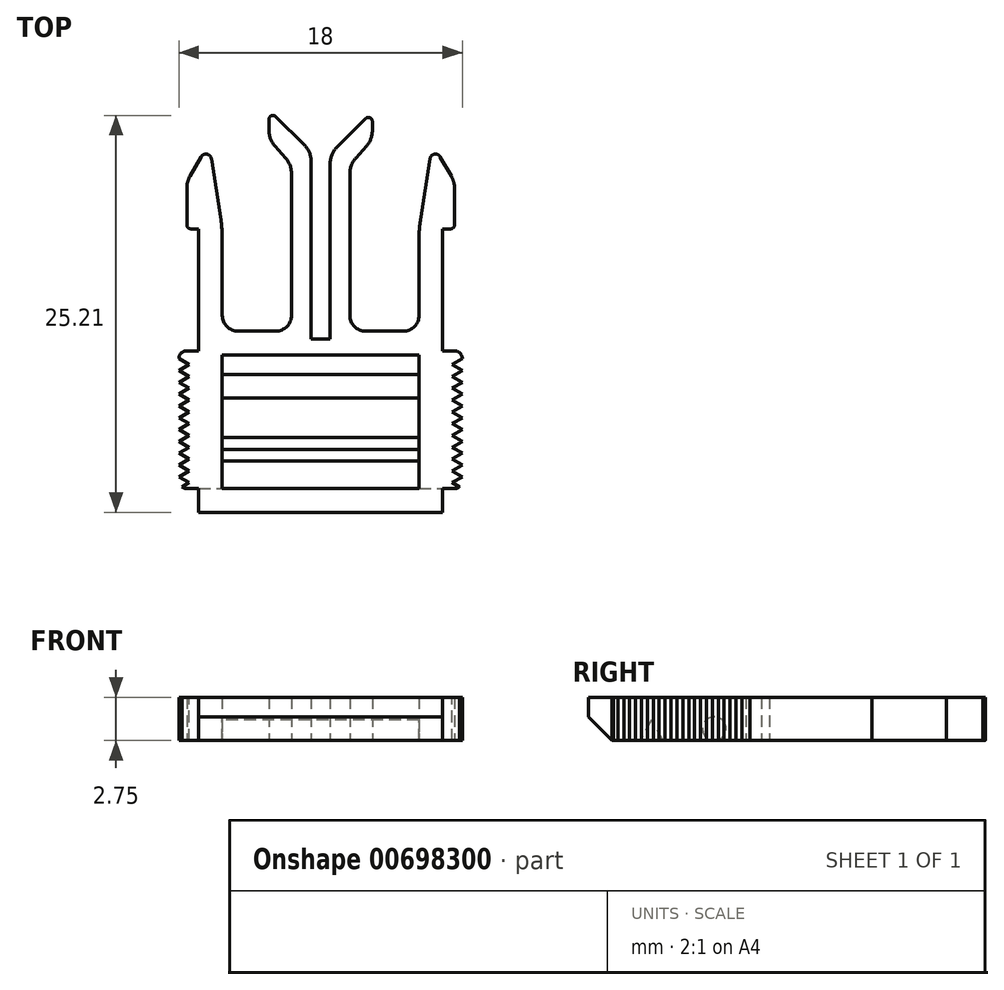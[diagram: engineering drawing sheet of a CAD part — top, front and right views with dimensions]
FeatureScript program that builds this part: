
annotation { "Feature Type Name" : "Feature", "Feature Type Description" : "" }
export const myFeature = defineFeature(function(context is Context, id is Id, definition is map)
    precondition{}
    {
        {
            var Q0;
            Q0=qCreatedBy(makeId("Top.planeOp"),FACE);
            var sketch = newSketch(context, id + "F0", { "sketchPlane" : qUnion([Q0])});
            skLineSegment(sketch, "E0.top", {"start": v(15.5, -24.35) * mm, "end": v(-15.5, -24.35) * mm});
            skPoint(sketch, "E0.middle", {"position": v(0, 0) * mm});
            skLineSegment(sketch, "E1.bottom", {"start": v(12.5, -4.35) * mm, "end": v(-12.5, -4.35) * mm});
            skLineSegment(sketch, "E1.top", {"start": v(12.5, -21.35) * mm, "end": v(-12.5, -21.35) * mm});
            skLineSegment(sketch, "E1.left", {"start": v(12.5, -4.35) * mm, "end": v(12.5, -21.35) * mm});
            skLineSegment(sketch, "E1.right", {"start": v(-12.5, -4.35) * mm, "end": v(-12.5, -21.35) * mm});
            skPoint(sketch, "E1.middle", {"position": v(0, -12.85) * mm});
            skLineSegment(sketch, "E2", {"start": v(15.18, 20.8) * mm, "end": v(16.6, 18.34) * mm});
            skLineSegment(sketch, "E3", {"start": v(17, 16.84) * mm, "end": v(17, 12.15) * mm});
            skLineSegment(sketch, "E4", {"start": v(16.5, 11.65) * mm, "end": v(15.5, 11.65) * mm});
            skLineSegment(sketch, "E5", {"start": v(0, -4.35) * mm, "end": v(0, 27.9) * mm, "construction": true});
            skLineSegment(sketch, "E6", {"start": v(-10.5, -1.35) * mm, "end": v(-5.7, -1.35) * mm});
            skLineSegment(sketch, "E7.trimOffspring", {"start": v(15.5, 11.65) * mm, "end": v(15.5, -24.35) * mm});
            skLineSegment(sketch, "E8", {"start": v(12.5, 10.49) * mm, "end": v(12.5, 0.65) * mm});
            skLineSegment(sketch, "E9.0", {"start": v(-3.7, 0.65) * mm, "end": v(-3.7, 18.65) * mm});
            skLineSegment(sketch, "E10.0", {"start": v(3.7, 0.65) * mm, "end": v(3.7, 18.65) * mm});
            skLineSegment(sketch, "E11", {"start": v(13.89, 20.55) * mm, "end": v(12.68, 12.8) * mm});
            skPoint(sketch, "E12.visualSharp", {"position": v(12.5, 11.65) * mm});
            skArc(sketch, "E12.filletArc", {"start": v(12.68, 12.8) * mm, "mid": v(12.54, 11.64) * mm, "end": v(12.5, 10.49) * mm});
            skLineSegment(sketch, "E13.trimOffspring", {"start": v(5.7, -1.35) * mm, "end": v(10.5, -1.35) * mm});
            skPoint(sketch, "E14.orphan", {"position": v(13.51, 18.14) * mm});
            skPoint(sketch, "E15.orphan", {"position": v(16.29, 18.88) * mm});
            skPoint(sketch, "E16.orphan", {"position": v(15.5, -1.35) * mm});
            skPoint(sketch, "E17.visualSharp", {"position": v(14.2, 22.51) * mm});
            skArc(sketch, "E17.filletArc", {"start": v(15.18, 20.8) * mm, "mid": v(14.45, 21.13) * mm, "end": v(13.89, 20.55) * mm});
            skArc(sketch, "E18.MirrorCS", {"start": v(-15.18, 20.8) * mm, "mid": v(-14.45, 21.13) * mm, "end": v(-13.89, 20.55) * mm});
            skLineSegment(sketch, "E19.MirrorCS", {"start": v(-15.18, 20.8) * mm, "end": v(-16.6, 18.34) * mm});
            skLineSegment(sketch, "E20.MirrorCS", {"start": v(-16.5, 11.65) * mm, "end": v(-15.5, 11.65) * mm});
            skPoint(sketch, "E21.MirrorP", {"position": v(-13.51, 18.14) * mm});
            skPoint(sketch, "E22.MirrorP", {"position": v(-12.5, 11.65) * mm});
            skArc(sketch, "E23.MirrorCS", {"start": v(-12.68, 12.8) * mm, "mid": v(-12.54, 11.64) * mm, "end": v(-12.5, 10.49) * mm});
            skPoint(sketch, "E24.MirrorP", {"position": v(-14.2, 22.51) * mm});
            skPoint(sketch, "E25.MirrorP", {"position": v(-16.29, 18.88) * mm});
            skLineSegment(sketch, "E26.MirrorCS", {"start": v(-17, 16.84) * mm, "end": v(-17, 12.15) * mm});
            skLineSegment(sketch, "E27.MirrorCS", {"start": v(-13.89, 20.55) * mm, "end": v(-12.68, 12.8) * mm});
            skLineSegment(sketch, "E28.MirrorCS", {"start": v(-15.5, 11.65) * mm, "end": v(-15.5, -24.35) * mm});
            skLineSegment(sketch, "E29.MirrorCS", {"start": v(-12.5, 10.49) * mm, "end": v(-12.5, 0.65) * mm});
            skLineSegment(sketch, "E30.0", {"start": v(1.2, -2.35) * mm, "end": v(1.2, 19.9) * mm});
            skLineSegment(sketch, "E31.0", {"start": v(-1.2, -2.35) * mm, "end": v(-1.2, 20.17) * mm});
            skLineSegment(sketch, "E32", {"start": v(5.7, 25.65) * mm, "end": v(2.08, 22.03) * mm});
            skLineSegment(sketch, "E33", {"start": v(-5.7, 25.92) * mm, "end": v(-2.08, 22.29) * mm});
            skPoint(sketch, "E34.visualSharp", {"position": v(17, 17.65) * mm});
            skArc(sketch, "E34.filletArc", {"start": v(17, 16.84) * mm, "mid": v(16.9, 17.62) * mm, "end": v(16.6, 18.34) * mm});
            skPoint(sketch, "E35.visualSharp", {"position": v(-17, 17.65) * mm});
            skArc(sketch, "E35.filletArc", {"start": v(-16.6, 18.34) * mm, "mid": v(-16.9, 17.62) * mm, "end": v(-17, 16.84) * mm});
            skLineSegment(sketch, "E36", {"start": v(-1.2, -2.35) * mm, "end": v(1.2, -2.35) * mm});
            skPoint(sketch, "E37.orphan", {"position": v(1.2, 0.65) * mm});
            skPoint(sketch, "E38.orphan", {"position": v(-1.2, 0.65) * mm});
            skLineSegment(sketch, "E39", {"start": v(4.46, 20.65) * mm, "end": v(5.8, 22.14) * mm});
            skLineSegment(sketch, "E40", {"start": v(6.56, 24.14) * mm, "end": v(6.56, 25.3) * mm});
            skLineSegment(sketch, "E41.MirrorCS", {"start": v(-4.46, 20.65) * mm, "end": v(-5.8, 22.14) * mm});
            skLineSegment(sketch, "E42.MirrorCS", {"start": v(-6.56, 24.14) * mm, "end": v(-6.56, 25.56) * mm});
            skPoint(sketch, "E43.newPointB", {"position": v(6.56, 27.77) * mm});
            skArc(sketch, "E43.filletArc", {"start": v(6.56, 25.3) * mm, "mid": v(6.25, 25.76) * mm, "end": v(5.7, 25.65) * mm});
            skPoint(sketch, "E44.newPointB", {"position": v(-6.56, 27.77) * mm});
            skArc(sketch, "E44.filletArc", {"start": v(-5.7, 25.92) * mm, "mid": v(-6.25, 26.03) * mm, "end": v(-6.56, 25.56) * mm});
            skPoint(sketch, "E45.orphan", {"position": v(3.7, 23.65) * mm});
            skPoint(sketch, "E46.orphan", {"position": v(-3.7, 23.91) * mm});
            skPoint(sketch, "E47.visualSharp", {"position": v(3.7, 19.8) * mm});
            skArc(sketch, "E47.filletArc", {"start": v(4.46, 20.65) * mm, "mid": v(3.9, 19.72) * mm, "end": v(3.7, 18.65) * mm});
            skPoint(sketch, "E48.visualSharp", {"position": v(1.2, 21.15) * mm});
            skArc(sketch, "E48.filletArc", {"start": v(2.08, 22.03) * mm, "mid": v(1.43, 21.05) * mm, "end": v(1.2, 19.9) * mm});
            skPoint(sketch, "E49.visualSharp", {"position": v(-1.2, 21.41) * mm});
            skArc(sketch, "E49.filletArc", {"start": v(-1.2, 20.17) * mm, "mid": v(-1.43, 21.32) * mm, "end": v(-2.08, 22.29) * mm});
            skPoint(sketch, "E50.visualSharp", {"position": v(-3.7, 19.8) * mm});
            skArc(sketch, "E50.filletArc", {"start": v(-3.7, 18.65) * mm, "mid": v(-3.9, 19.72) * mm, "end": v(-4.46, 20.65) * mm});
            skPoint(sketch, "E51.visualSharp", {"position": v(6.56, 23) * mm});
            skArc(sketch, "E51.filletArc", {"start": v(5.8, 22.14) * mm, "mid": v(6.36, 23.07) * mm, "end": v(6.56, 24.14) * mm});
            skPoint(sketch, "E52.visualSharp", {"position": v(-6.56, 23) * mm});
            skArc(sketch, "E52.filletArc", {"start": v(-6.56, 24.14) * mm, "mid": v(-6.36, 23.07) * mm, "end": v(-5.8, 22.14) * mm});
            skPoint(sketch, "E53.visualSharp", {"position": v(12.5, -1.35) * mm});
            skArc(sketch, "E53.filletArc", {"start": v(10.5, -1.35) * mm, "mid": v(11.91, -0.77) * mm, "end": v(12.5, 0.65) * mm});
            skPoint(sketch, "E54.visualSharp", {"position": v(-12.5, -1.35) * mm});
            skArc(sketch, "E54.filletArc", {"start": v(-12.5, 0.65) * mm, "mid": v(-11.91, -0.77) * mm, "end": v(-10.5, -1.35) * mm});
            skPoint(sketch, "E55.visualSharp", {"position": v(-3.7, -1.35) * mm});
            skArc(sketch, "E55.filletArc", {"start": v(-5.7, -1.35) * mm, "mid": v(-4.29, -0.77) * mm, "end": v(-3.7, 0.65) * mm});
            skPoint(sketch, "E56.visualSharp", {"position": v(3.7, -1.35) * mm});
            skArc(sketch, "E56.filletArc", {"start": v(3.7, 0.65) * mm, "mid": v(4.29, -0.77) * mm, "end": v(5.7, -1.35) * mm});
            skPoint(sketch, "E57.visualSharp", {"position": v(17, 11.65) * mm});
            skArc(sketch, "E57.filletArc", {"start": v(16.5, 11.65) * mm, "mid": v(16.85, 11.8) * mm, "end": v(17, 12.15) * mm});
            skPoint(sketch, "E58.visualSharp", {"position": v(-17, 11.65) * mm});
            skArc(sketch, "E58.filletArc", {"start": v(-17, 12.15) * mm, "mid": v(-16.85, 11.8) * mm, "end": v(-16.5, 11.65) * mm});
            skSolve(sketch);
        }
        {
            var Q0;
            Q0=makeQuery(id+"F0.imprint","IMPRINT",FACE,{"disambiguationData":[TD([[makeQuery(id+"F0.imprint","IMPRINT",EDGE,{"derivedFrom":sQuery(id+"F0.wireOp",EDGE,"E0.top")}),-1.0]])]});
            extrude(context, id + "F1", {"entities" : qUnion([Q0]), "depth" : 5.5 * mm});
        }
        {
            var Q0;
            Q0=makeQuery(id+"F1.opExtrude","SWEPT_FACE",FACE,{"disambiguationData":[OSD([sQuery(id+"F0.wireOp",EDGE,"E1.right")])]});
            var sketch = newSketch(context, id + "F2", { "sketchPlane" : qUnion([Q0])});
            skLineSegment(sketch, "E59", {"start": v(-16.35, 2.6) * mm, "end": v(-17.85, 0) * mm});
            skLineSegment(sketch, "E60", {"start": v(-17.85, 0) * mm, "end": v(-14.85, 0) * mm});
            skLineSegment(sketch, "E61", {"start": v(-14.85, 0) * mm, "end": v(-16.35, 2.6) * mm});
            skCircle(sketch, "E62", {"center": v(-8.35, 1.5) * mm, "radius": 1.5 * mm});
            skPoint(sketch, "E62.centerSnap0", {"position": v(-4.35, 2.75) * mm});
            skSolve(sketch);
        }
        {
            var Q0;
            Q0=makeQuery(id+"F2.imprint","IMPRINT",FACE,{"disambiguationData":[TD([[makeQuery(id+"F2.imprint","IMPRINT",EDGE,{"derivedFrom":sQuery(id+"F2.wireOp",EDGE,"E59")}),1.0]])]});
            var Q1;
            Q1=makeQuery(id+"F2.imprint","IMPRINT",FACE,{"disambiguationData":[TD([[makeQuery(id+"F2.imprint","IMPRINT",EDGE,{"derivedFrom":sQuery(id+"F2.wireOp",EDGE,"E62")}),1.0]])]});
            extrude(context, id + "F3", {"entities" : qUnion([Q0, Q1]), "operationType" : NewBodyOperationType.ADD, "depth" : 25 * mm});
        }
        {
            var Q0;
            Q0=makeQuery(id+"F1.opExtrude","SWEPT_FACE",FACE,{"disambiguationData":[OSD([sQuery(id+"F0.wireOp",EDGE,"E7.trimOffspring")])]});
            var sketch = newSketch(context, id + "F4", { "sketchPlane" : qUnion([Q0])});
            skLineSegment(sketch, "E63", {"start": v(-21.35, 0) * mm, "end": v(-24.35, 3) * mm});
            skSolve(sketch);
        }
        {
            var Q0;
            {var subQ0=sQuery(id+"F4.wireOp",EDGE,"E63");Q0=makeQuery(id+"F4.imprint","IMPRINT",FACE,{"disambiguationData":[TD([[makeQuery(id+"F4.imprint","IMPRINT",EDGE,{"derivedFrom":subQ0}),1.0]])]});}
            var Q1;
            Q1=makeQuery(id+"F1.opExtrude","SWEPT_FACE",FACE,{"disambiguationData":[OSD([sQuery(id+"F0.wireOp",EDGE,"E1.right")])]});
            var Q2;
            Q2=makeQuery(id+"F1.opExtrude","SWEPT_FACE",FACE,{"disambiguationData":[OSD([sQuery(id+"F0.wireOp",EDGE,"E1.left")])]});
            extrude(context, id + "F5", {"entities" : qUnion([Q0]), "operationType" : NewBodyOperationType.REMOVE, "endBound" : BoundingType.THROUGH_ALL, "oppositeDirection" : true, "endBoundEntityFace" : qUnion([Q1]), "depth" : 25 * mm});
        }
        {
            var Q0;
            Q0=makeQuery(id+"F1.opExtrude","CAP_FACE",FACE,{"disambiguationData":[OSD([sQuery(id+"F0.wireOp",EDGE,"E0.top"),sQuery(id+"F0.wireOp",EDGE,"E1.bottom"),sQuery(id+"F0.wireOp",EDGE,"E1.top"),sQuery(id+"F0.wireOp",EDGE,"E1.left"),sQuery(id+"F0.wireOp",EDGE,"E1.right"),sQuery(id+"F0.wireOp",EDGE,"E2"),sQuery(id+"F0.wireOp",EDGE,"E3"),sQuery(id+"F0.wireOp",EDGE,"E4"),sQuery(id+"F0.wireOp",EDGE,"E6"),sQuery(id+"F0.wireOp",EDGE,"E7.trimOffspring"),sQuery(id+"F0.wireOp",EDGE,"E8"),sQuery(id+"F0.wireOp",EDGE,"E9.0"),sQuery(id+"F0.wireOp",EDGE,"E10.0"),sQuery(id+"F0.wireOp",EDGE,"E11"),sQuery(id+"F0.wireOp",EDGE,"E12.filletArc"),sQuery(id+"F0.wireOp",EDGE,"E13.trimOffspring"),sQuery(id+"F0.wireOp",EDGE,"E17.filletArc"),sQuery(id+"F0.wireOp",EDGE,"E18.MirrorCS"),sQuery(id+"F0.wireOp",EDGE,"E19.MirrorCS"),sQuery(id+"F0.wireOp",EDGE,"E20.MirrorCS"),sQuery(id+"F0.wireOp",EDGE,"E23.MirrorCS"),sQuery(id+"F0.wireOp",EDGE,"E26.MirrorCS"),sQuery(id+"F0.wireOp",EDGE,"E27.MirrorCS"),sQuery(id+"F0.wireOp",EDGE,"E28.MirrorCS"),sQuery(id+"F0.wireOp",EDGE,"E29.MirrorCS"),sQuery(id+"F0.wireOp",EDGE,"E30.0"),sQuery(id+"F0.wireOp",EDGE,"E31.0"),sQuery(id+"F0.wireOp",EDGE,"UTjdTIHE-D38J-cQlS-tRNC-KbjzHWpZoidh"),sQuery(id+"F0.wireOp",EDGE,"E32"),sQuery(id+"F0.wireOp",EDGE,"E33"),sQuery(id+"F0.wireOp",EDGE,"E34.filletArc"),sQuery(id+"F0.wireOp",EDGE,"E35.filletArc")])],"isStart":false});
            var sketch = newSketch(context, id + "F6", { "sketchPlane" : qUnion([Q0])});
            skLineSegment(sketch, "E64", {"start": v(15.5, -3.85) * mm, "end": v(17, -3.85) * mm});
            skLineSegment(sketch, "E65", {"start": v(18, -4.85) * mm, "end": v(18, -20.35) * mm});
            skLineSegment(sketch, "E66", {"start": v(17, -21.35) * mm, "end": v(15.5, -21.35) * mm});
            skPoint(sketch, "E67.visualSharp", {"position": v(18, -3.85) * mm});
            skArc(sketch, "E67.filletArc", {"start": v(18, -4.85) * mm, "mid": v(17.7, -4.15) * mm, "end": v(17, -3.85) * mm});
            skPoint(sketch, "E68.visualSharp", {"position": v(18, -21.35) * mm});
            skArc(sketch, "E68.filletArc", {"start": v(17, -21.35) * mm, "mid": v(17.7, -21.06) * mm, "end": v(18, -20.35) * mm});
            skLineSegment(sketch, "E69", {"start": v(15.5, -3.85) * mm, "end": v(15.5, -21.35) * mm});
            skSolve(sketch);
        }
        {
            var Q0;
            Q0=makeQuery(id+"F6.imprint","IMPRINT",FACE,{"disambiguationData":[TD([[makeQuery(id+"F6.imprint","IMPRINT",EDGE,{"derivedFrom":sQuery(id+"F6.wireOp",EDGE,"E64")}),-1.0]])]});
            var Q1;
            Q1=makeQuery(id+"F1.opExtrude","CAP_FACE",FACE,{"disambiguationData":[OSD([sQuery(id+"F0.wireOp",EDGE,"E0.top"),sQuery(id+"F0.wireOp",EDGE,"E1.bottom"),sQuery(id+"F0.wireOp",EDGE,"E1.top"),sQuery(id+"F0.wireOp",EDGE,"E1.left"),sQuery(id+"F0.wireOp",EDGE,"E1.right"),sQuery(id+"F0.wireOp",EDGE,"E2"),sQuery(id+"F0.wireOp",EDGE,"E3"),sQuery(id+"F0.wireOp",EDGE,"E4"),sQuery(id+"F0.wireOp",EDGE,"E6"),sQuery(id+"F0.wireOp",EDGE,"E7.trimOffspring"),sQuery(id+"F0.wireOp",EDGE,"E8"),sQuery(id+"F0.wireOp",EDGE,"E9.0"),sQuery(id+"F0.wireOp",EDGE,"E10.0"),sQuery(id+"F0.wireOp",EDGE,"E11"),sQuery(id+"F0.wireOp",EDGE,"E12.filletArc"),sQuery(id+"F0.wireOp",EDGE,"E13.trimOffspring"),sQuery(id+"F0.wireOp",EDGE,"E17.filletArc"),sQuery(id+"F0.wireOp",EDGE,"E18.MirrorCS"),sQuery(id+"F0.wireOp",EDGE,"E19.MirrorCS"),sQuery(id+"F0.wireOp",EDGE,"E20.MirrorCS"),sQuery(id+"F0.wireOp",EDGE,"E23.MirrorCS"),sQuery(id+"F0.wireOp",EDGE,"E26.MirrorCS"),sQuery(id+"F0.wireOp",EDGE,"E27.MirrorCS"),sQuery(id+"F0.wireOp",EDGE,"E28.MirrorCS"),sQuery(id+"F0.wireOp",EDGE,"E29.MirrorCS"),sQuery(id+"F0.wireOp",EDGE,"E30.0"),sQuery(id+"F0.wireOp",EDGE,"E31.0"),sQuery(id+"F0.wireOp",EDGE,"UTjdTIHE-D38J-cQlS-tRNC-KbjzHWpZoidh"),sQuery(id+"F0.wireOp",EDGE,"E32"),sQuery(id+"F0.wireOp",EDGE,"E33"),sQuery(id+"F0.wireOp",EDGE,"E34.filletArc"),sQuery(id+"F0.wireOp",EDGE,"E35.filletArc")])],"isStart":true});
            extrude(context, id + "F7", {"entities" : qUnion([Q0]), "endBound" : BoundingType.UP_TO_SURFACE, "oppositeDirection" : true, "endBoundEntityFace" : qUnion([Q1]), "depth" : 25 * mm});
        }
        {
            var Q0;
            Q0=makeQuery(id+"F7.opExtrude","CAP_FACE",FACE,{"disambiguationData":[OSD([sQuery(id+"F6.wireOp",EDGE,"E64"),sQuery(id+"F6.wireOp",EDGE,"E65"),sQuery(id+"F6.wireOp",EDGE,"E66"),sQuery(id+"F6.wireOp",EDGE,"E67.filletArc"),sQuery(id+"F6.wireOp",EDGE,"E68.filletArc"),sQuery(id+"F6.wireOp",EDGE,"E69")])],"isStart":true});
            var sketch = newSketch(context, id + "F8", { "sketchPlane" : qUnion([Q0])});
            skLineSegment(sketch, "E70", {"start": v(18, -4.85) * mm, "end": v(16.7, -5.6) * mm});
            skLineSegment(sketch, "E71", {"start": v(16.7, -5.6) * mm, "end": v(18, -6.35) * mm});
            skLineSegment(sketch, "E72", {"start": v(18, -6.35) * mm, "end": v(18, -4.85) * mm});
            skLineSegment(sketch, "E73.0.1.0", {"start": v(18, -7.85) * mm, "end": v(18, -6.35) * mm});
            skLineSegment(sketch, "E73.0.1.1", {"start": v(16.7, -7.1) * mm, "end": v(18, -7.85) * mm});
            skLineSegment(sketch, "E73.0.1.2", {"start": v(18, -6.35) * mm, "end": v(16.7, -7.1) * mm});
            skLineSegment(sketch, "E73.0.2.0", {"start": v(18, -9.35) * mm, "end": v(18, -7.85) * mm});
            skLineSegment(sketch, "E73.0.2.1", {"start": v(16.7, -8.6) * mm, "end": v(18, -9.35) * mm});
            skLineSegment(sketch, "E73.0.2.2", {"start": v(18, -7.85) * mm, "end": v(16.7, -8.6) * mm});
            skLineSegment(sketch, "E73.0.3.0", {"start": v(18, -10.85) * mm, "end": v(18, -9.35) * mm});
            skLineSegment(sketch, "E73.0.3.1", {"start": v(16.7, -10.1) * mm, "end": v(18, -10.85) * mm});
            skLineSegment(sketch, "E73.0.3.2", {"start": v(18, -9.35) * mm, "end": v(16.7, -10.1) * mm});
            skLineSegment(sketch, "E73.0.4.0", {"start": v(18, -12.35) * mm, "end": v(18, -10.85) * mm});
            skLineSegment(sketch, "E73.0.4.1", {"start": v(16.7, -11.6) * mm, "end": v(18, -12.35) * mm});
            skLineSegment(sketch, "E73.0.4.2", {"start": v(18, -10.85) * mm, "end": v(16.7, -11.6) * mm});
            skLineSegment(sketch, "E73.0.5.0", {"start": v(18, -13.85) * mm, "end": v(18, -12.35) * mm});
            skLineSegment(sketch, "E73.0.5.1", {"start": v(16.7, -13.1) * mm, "end": v(18, -13.85) * mm});
            skLineSegment(sketch, "E73.0.5.2", {"start": v(18, -12.35) * mm, "end": v(16.7, -13.1) * mm});
            skLineSegment(sketch, "E73.0.6.0", {"start": v(18, -15.35) * mm, "end": v(18, -13.85) * mm});
            skLineSegment(sketch, "E73.0.6.1", {"start": v(16.7, -14.6) * mm, "end": v(18, -15.35) * mm});
            skLineSegment(sketch, "E73.0.6.2", {"start": v(18, -13.85) * mm, "end": v(16.7, -14.6) * mm});
            skLineSegment(sketch, "E73.0.7.0", {"start": v(18, -16.85) * mm, "end": v(18, -15.35) * mm});
            skLineSegment(sketch, "E73.0.7.1", {"start": v(16.7, -16.1) * mm, "end": v(18, -16.85) * mm});
            skLineSegment(sketch, "E73.0.7.2", {"start": v(18, -15.35) * mm, "end": v(16.7, -16.1) * mm});
            skLineSegment(sketch, "E73.0.8.0", {"start": v(18, -18.35) * mm, "end": v(18, -16.85) * mm});
            skLineSegment(sketch, "E73.0.8.1", {"start": v(16.7, -17.6) * mm, "end": v(18, -18.35) * mm});
            skLineSegment(sketch, "E73.0.8.2", {"start": v(18, -16.85) * mm, "end": v(16.7, -17.6) * mm});
            skLineSegment(sketch, "E73.0.9.0", {"start": v(18, -19.85) * mm, "end": v(18, -18.35) * mm});
            skLineSegment(sketch, "E73.0.9.1", {"start": v(16.7, -19.1) * mm, "end": v(18, -19.85) * mm});
            skLineSegment(sketch, "E73.0.9.2", {"start": v(18, -18.35) * mm, "end": v(16.7, -19.1) * mm});
            skLineSegment(sketch, "E73.0.10.0", {"start": v(18, -21.35) * mm, "end": v(18, -19.85) * mm});
            skLineSegment(sketch, "E73.0.10.1", {"start": v(16.7, -20.6) * mm, "end": v(18, -21.35) * mm});
            skLineSegment(sketch, "E73.0.10.2", {"start": v(18, -19.85) * mm, "end": v(16.7, -20.6) * mm});
            skLineSegment(sketch, "E73.direction1", {"start": v(18, -6.35) * mm, "end": v(36.9, -6.35) * mm, "construction": true});
            skLineSegment(sketch, "E73.direction2", {"start": v(18, -6.35) * mm, "end": v(18, -7.85) * mm, "construction": true});
            skLineSegment(sketch, "E74", {"start": v(0, 0) * mm, "end": v(0, -26.7) * mm, "construction": true});
            skSolve(sketch);
        }
        {
            var Q0;
            Q0=qSketchRegion(id+"F8",true);
            extrude(context, id + "F9", {"entities" : qUnion([Q0]), "operationType" : NewBodyOperationType.REMOVE, "endBound" : BoundingType.THROUGH_ALL, "oppositeDirection" : true, "depth" : 25 * mm});
        }
        {
            var Q0;
            Q0=makeQuery(id+"F1.opExtrude","SWEPT_FACE",FACE,{"disambiguationData":[OSD([sQuery(id+"F0.wireOp",EDGE,"E7.trimOffspring")])]});
            var Q1;
            Q1=makeQuery(id+"F1.opExtrude","SWEPT_FACE",FACE,{"disambiguationData":[OSD([sQuery(id+"F0.wireOp",EDGE,"E28.MirrorCS")])]});
            cPlane(context, id + "F10", {"entities" : qUnion([Q0, Q1]), "cplaneType" : CPlaneType.MID_PLANE, "offset" : 150 * mm, "width" : 150 * mm, "height" : 150 * mm});
        }
        {
            var Q0;
            Q0=makeQuery(id+"F7.opExtrude","SWEPT_BODY",BODY,{"disambiguationData":[OSD([sQuery(id+"F6.wireOp",EDGE,"E64"),sQuery(id+"F6.wireOp",EDGE,"E65"),sQuery(id+"F6.wireOp",EDGE,"E66"),sQuery(id+"F6.wireOp",EDGE,"E67.filletArc"),sQuery(id+"F6.wireOp",EDGE,"E68.filletArc"),sQuery(id+"F6.wireOp",EDGE,"E69")])]});
            var Q1;
            Q1=qCreatedBy(id+"F10.planeOp",FACE);
            mirror(context, id + "F11", {"operationType" : NewBodyOperationType.ADD, "entities" : qUnion([Q0]), "mirrorPlane" : qUnion([Q1])});
        }
        {
            var Q0;
            Q0=makeQuery(id+"F1.opExtrude","SWEPT_BODY",BODY,{"disambiguationData":[OSD([sQuery(id+"F0.wireOp",EDGE,"E0.top"),sQuery(id+"F0.wireOp",EDGE,"E1.bottom"),sQuery(id+"F0.wireOp",EDGE,"E1.top"),sQuery(id+"F0.wireOp",EDGE,"E1.left"),sQuery(id+"F0.wireOp",EDGE,"E1.right"),sQuery(id+"F0.wireOp",EDGE,"E2"),sQuery(id+"F0.wireOp",EDGE,"E3"),sQuery(id+"F0.wireOp",EDGE,"E4"),sQuery(id+"F0.wireOp",EDGE,"E6"),sQuery(id+"F0.wireOp",EDGE,"E7.trimOffspring"),sQuery(id+"F0.wireOp",EDGE,"E8"),sQuery(id+"F0.wireOp",EDGE,"E9.0"),sQuery(id+"F0.wireOp",EDGE,"E10.0"),sQuery(id+"F0.wireOp",EDGE,"E11"),sQuery(id+"F0.wireOp",EDGE,"E12.filletArc"),sQuery(id+"F0.wireOp",EDGE,"E13.trimOffspring"),sQuery(id+"F0.wireOp",EDGE,"E17.filletArc"),sQuery(id+"F0.wireOp",EDGE,"E18.MirrorCS"),sQuery(id+"F0.wireOp",EDGE,"E19.MirrorCS"),sQuery(id+"F0.wireOp",EDGE,"E20.MirrorCS"),sQuery(id+"F0.wireOp",EDGE,"E23.MirrorCS"),sQuery(id+"F0.wireOp",EDGE,"E26.MirrorCS"),sQuery(id+"F0.wireOp",EDGE,"E27.MirrorCS"),sQuery(id+"F0.wireOp",EDGE,"E28.MirrorCS"),sQuery(id+"F0.wireOp",EDGE,"E29.MirrorCS"),sQuery(id+"F0.wireOp",EDGE,"E30.0"),sQuery(id+"F0.wireOp",EDGE,"E31.0"),sQuery(id+"F0.wireOp",EDGE,"E32"),sQuery(id+"F0.wireOp",EDGE,"E33"),sQuery(id+"F0.wireOp",EDGE,"E34.filletArc"),sQuery(id+"F0.wireOp",EDGE,"E35.filletArc"),sQuery(id+"F0.wireOp",EDGE,"E36"),sQuery(id+"F0.wireOp",EDGE,"E39"),sQuery(id+"F0.wireOp",EDGE,"E40"),sQuery(id+"F0.wireOp",EDGE,"E41.MirrorCS"),sQuery(id+"F0.wireOp",EDGE,"E42.MirrorCS"),sQuery(id+"F0.wireOp",EDGE,"E43.filletArc"),sQuery(id+"F0.wireOp",EDGE,"E44.filletArc"),sQuery(id+"F0.wireOp",EDGE,"E47.filletArc"),sQuery(id+"F0.wireOp",EDGE,"E48.filletArc"),sQuery(id+"F0.wireOp",EDGE,"E49.filletArc"),sQuery(id+"F0.wireOp",EDGE,"E50.filletArc"),sQuery(id+"F0.wireOp",EDGE,"E51.filletArc"),sQuery(id+"F0.wireOp",EDGE,"E52.filletArc"),sQuery(id+"F0.wireOp",EDGE,"E53.filletArc"),sQuery(id+"F0.wireOp",EDGE,"E54.filletArc"),sQuery(id+"F0.wireOp",EDGE,"E55.filletArc"),sQuery(id+"F0.wireOp",EDGE,"E56.filletArc"),sQuery(id+"F0.wireOp",EDGE,"E57.filletArc"),sQuery(id+"F0.wireOp",EDGE,"E58.filletArc")])]});
            var Q1;
            Q1=sQuery(id+"F0.wireOp",VERTEX,"E5.end");
            transform(context, id + "F12", {"entities" : qUnion([Q0]), "transformType" : TransformType.SCALE_UNIFORMLY, "scale" : .5, "scalePoint" : qUnion([Q1]), "makeCopy" : false});
        }
    });
